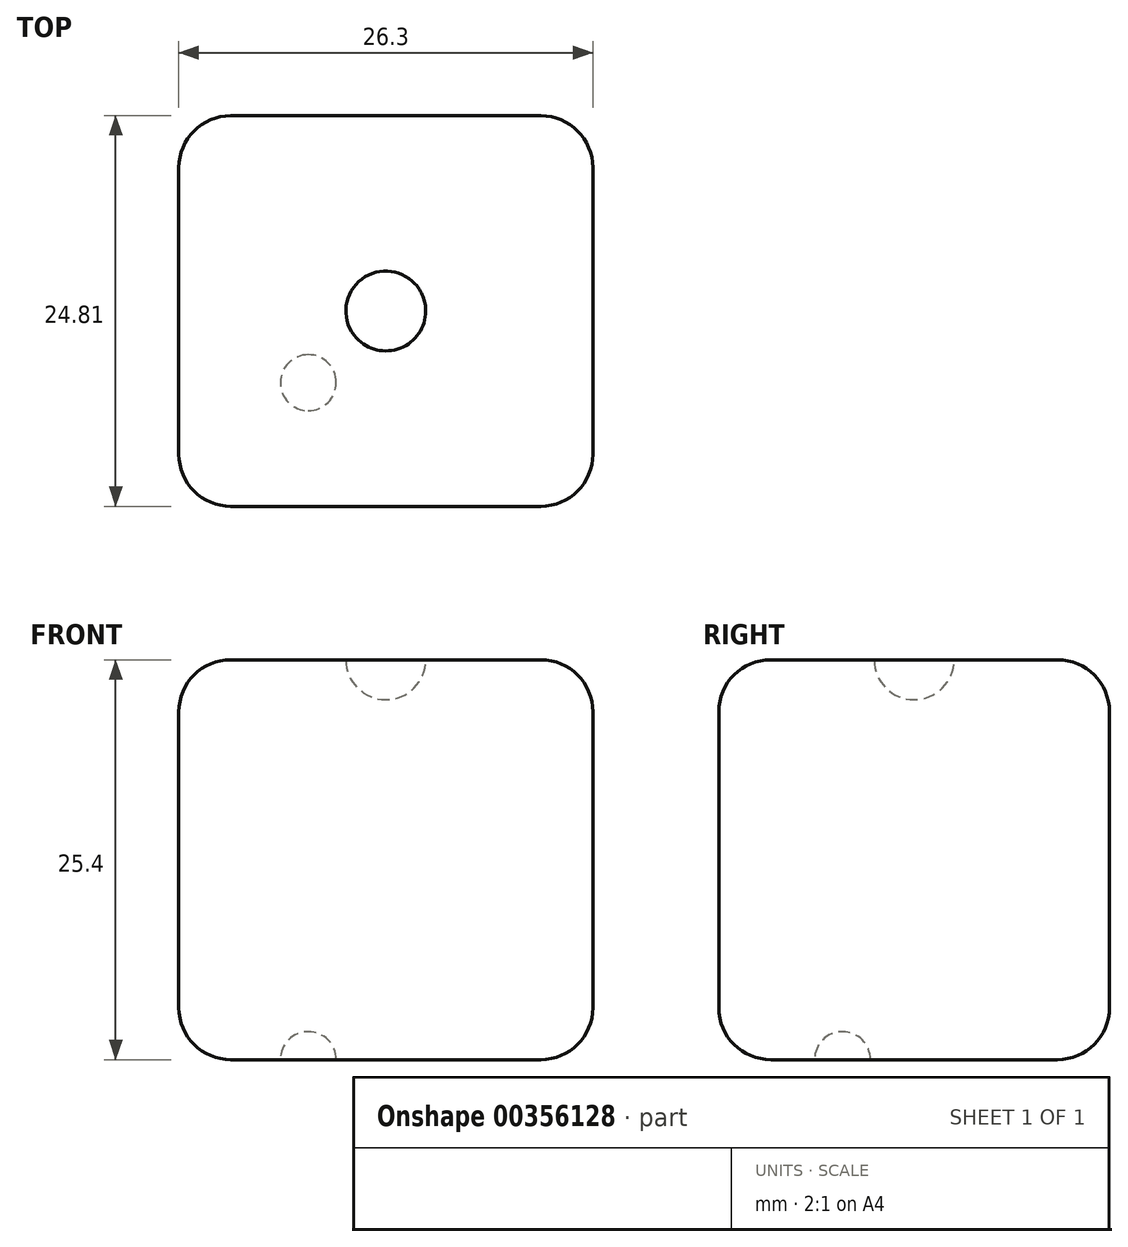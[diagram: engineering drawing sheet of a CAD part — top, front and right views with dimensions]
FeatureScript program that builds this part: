
annotation { "Feature Type Name" : "Feature", "Feature Type Description" : "" }
export const myFeature = defineFeature(function(context is Context, id is Id, definition is map)
    precondition{}
    {
        {
            var Q0;
            Q0=qCreatedBy(makeId("Top.planeOp"),FACE);
            var sketch = newSketch(context, id + "F0", { "sketchPlane" : qUnion([Q0])});
            skLineSegment(sketch, "E0.bottom", {"start": v(35.97, 40.2) * mm, "end": v(62.27, 40.2) * mm});
            skLineSegment(sketch, "E0.top", {"start": v(35.97, 15.4) * mm, "end": v(62.27, 15.4) * mm});
            skLineSegment(sketch, "E0.left", {"start": v(35.97, 40.2) * mm, "end": v(35.97, 15.4) * mm});
            skLineSegment(sketch, "E0.right", {"start": v(62.27, 40.2) * mm, "end": v(62.27, 15.4) * mm});
            skSolve(sketch);
        }
        {
            var Q0;
            Q0=makeQuery(id+"F0.imprint","IMPRINT",FACE,{"disambiguationData":[TD([[makeQuery(id+"F0.imprint","IMPRINT",EDGE,{"derivedFrom":sQuery(id+"F0.wireOp",EDGE,"E0.bottom")}),-1.0]])]});
            extrude(context, id + "F1", {"entities" : qUnion([Q0]), "depth" : 25.4 * mm});
        }
        {
            var Q0;
            Q0=makeQuery(id+"F1.opExtrude","CAP_EDGE",EDGE,{"disambiguationData":[OSD([sQuery(id+"F0.wireOp",EDGE,"E0.top")])],"isStart":false});
            var Q1;
            Q1=makeQuery(id+"F1.opExtrude","CAP_EDGE",EDGE,{"disambiguationData":[OSD([sQuery(id+"F0.wireOp",EDGE,"E0.right")])],"isStart":false});
            var Q2;
            Q2=makeQuery(id+"F1.opExtrude","CAP_EDGE",EDGE,{"disambiguationData":[OSD([sQuery(id+"F0.wireOp",EDGE,"E0.bottom")])],"isStart":false});
            var Q3;
            Q3=makeQuery(id+"F1.opExtrude","CAP_EDGE",EDGE,{"disambiguationData":[OSD([sQuery(id+"F0.wireOp",EDGE,"E0.left")])],"isStart":false});
            var Q4;
            Q4=makeQuery(id+"F1.opExtrude","SWEPT_EDGE",EDGE,{"disambiguationData":[OSD([sQuery(id+"F0.wireOp",EDGE,"E0.bottom"),sQuery(id+"F0.wireOp",EDGE,"E0.right")])]});
            var Q5;
            Q5=makeQuery(id+"F1.opExtrude","CAP_EDGE",EDGE,{"disambiguationData":[OSD([sQuery(id+"F0.wireOp",EDGE,"E0.right")])],"isStart":true});
            var Q6;
            Q6=makeQuery(id+"F1.opExtrude","CAP_EDGE",EDGE,{"disambiguationData":[OSD([sQuery(id+"F0.wireOp",EDGE,"E0.bottom")])],"isStart":true});
            var Q7;
            Q7=makeQuery(id+"F1.opExtrude","SWEPT_EDGE",EDGE,{"disambiguationData":[OSD([sQuery(id+"F0.wireOp",EDGE,"E0.bottom"),sQuery(id+"F0.wireOp",EDGE,"E0.left")])]});
            var Q8;
            Q8=makeQuery(id+"F1.opExtrude","CAP_EDGE",EDGE,{"disambiguationData":[OSD([sQuery(id+"F0.wireOp",EDGE,"E0.top")])],"isStart":true});
            var Q9;
            Q9=makeQuery(id+"F1.opExtrude","CAP_EDGE",EDGE,{"disambiguationData":[OSD([sQuery(id+"F0.wireOp",EDGE,"E0.left")])],"isStart":true});
            var Q10;
            Q10=makeQuery(id+"F1.opExtrude","SWEPT_EDGE",EDGE,{"disambiguationData":[OSD([sQuery(id+"F0.wireOp",EDGE,"E0.top"),sQuery(id+"F0.wireOp",EDGE,"E0.left")])]});
            var Q11;
            Q11=makeQuery(id+"F1.opExtrude","SWEPT_EDGE",EDGE,{"disambiguationData":[OSD([sQuery(id+"F0.wireOp",EDGE,"E0.top"),sQuery(id+"F0.wireOp",EDGE,"E0.right")])]});
            fillet(context, id + "F2", {"entities" : qUnion([Q0, Q1, Q2, Q3, Q4, Q5, Q6, Q7, Q8, Q9, Q10, Q11]), "radius" : 3.3 * mm, "tangentPropagation" : true, "allowEdgeOverflow" : false});
        }
        {
            var Q0;
            Q0=makeQuery(id+"F1.opExtrude","CAP_FACE",FACE,{"disambiguationData":[OSD([sQuery(id+"F0.wireOp",EDGE,"E0.bottom"),sQuery(id+"F0.wireOp",EDGE,"E0.top"),sQuery(id+"F0.wireOp",EDGE,"E0.left"),sQuery(id+"F0.wireOp",EDGE,"E0.right")])],"isStart":false});
            var sketch = newSketch(context, id + "F3", { "sketchPlane" : qUnion([Q0])});
            skLineSegment(sketch, "E1", {"start": v(39.27, 18.7) * mm, "end": v(58.97, 36.9) * mm});
            skCircle(sketch, "E2", {"center": v(49.12, 27.8) * mm, "radius": 2.53 * mm});
            skSolve(sketch);
        }
        {
            var Q0;
            {var subQ0=sQuery(id+"F3.wireOp",EDGE,"E2");var subQ1=sQuery(id+"F3.wireOp",EDGE,"E1");var subQ2=makeQuery(id+"F3.imprint","INTERSECT",VERTEX,{"disambiguationData":[OD(0.0)],"derivedFrom":[subQ1,subQ0]});Q0=makeQuery(id+"F3.imprint","IMPRINT",FACE,{"disambiguationData":[TD([[makeQuery(id+"F3.imprint","IMPRINT",EDGE,{"disambiguationData":[TD([[subQ2,-1.0]])],"derivedFrom":subQ1}),1.0]])]});}
            var Q1;
            Q1=sQuery(id+"F3.wireOp",EDGE,"E1");
            revolve(context, id + "F4", {"operationType" : NewBodyOperationType.REMOVE, "entities" : qUnion([Q0]), "axis" : qUnion([Q1]), "revolveType" : RevolveType.TWO_DIRECTIONS, "angle" : 0 * degree, "angleBack" : 180 * degree});
        }
        {
            var Q0;
            Q0=makeQuery(id+"F1.opExtrude","CAP_FACE",FACE,{"disambiguationData":[OSD([sQuery(id+"F0.wireOp",EDGE,"E0.bottom"),sQuery(id+"F0.wireOp",EDGE,"E0.top"),sQuery(id+"F0.wireOp",EDGE,"E0.left"),sQuery(id+"F0.wireOp",EDGE,"E0.right")])],"isStart":true});
            var sketch = newSketch(context, id + "F5", { "sketchPlane" : qUnion([Q0])});
            skLineSegment(sketch, "E3", {"start": v(39.27, -18.7) * mm, "end": v(49.12, -18.7) * mm});
            skLineSegment(sketch, "E4", {"start": v(49.12, -18.7) * mm, "end": v(58.97, -18.7) * mm});
            skLineSegment(sketch, "E5", {"start": v(39.27, -27.8) * mm, "end": v(58.97, -27.8) * mm});
            skLineSegment(sketch, "E6", {"start": v(44.2, -18.7) * mm, "end": v(44.2, -27.8) * mm});
            skLineSegment(sketch, "E7", {"start": v(44.2, -27.8) * mm, "end": v(44.2, -36.9) * mm});
            skLineSegment(sketch, "E8", {"start": v(54.04, -18.7) * mm, "end": v(54.04, -27.8) * mm});
            skLineSegment(sketch, "E9", {"start": v(54.04, -27.8) * mm, "end": v(54.04, -36.9) * mm});
            skLineSegment(sketch, "E10", {"start": v(39.27, -18.7) * mm, "end": v(39.27, -27.8) * mm});
            skLineSegment(sketch, "E11", {"start": v(39.27, -27.8) * mm, "end": v(39.27, -36.9) * mm});
            skLineSegment(sketch, "E12", {"start": v(39.27, -23.24) * mm, "end": v(44.2, -23.24) * mm});
            skLineSegment(sketch, "E13", {"start": v(44.2, -23.24) * mm, "end": v(54.04, -23.24) * mm});
            skLineSegment(sketch, "E14", {"start": v(54.04, -23.24) * mm, "end": v(58.97, -23.24) * mm});
            skLineSegment(sketch, "E15", {"start": v(39.27, -31.88) * mm, "end": v(44.2, -31.88) * mm});
            skLineSegment(sketch, "E16", {"start": v(44.2, -31.88) * mm, "end": v(54.04, -31.88) * mm});
            skLineSegment(sketch, "E17", {"start": v(54.04, -31.88) * mm, "end": v(58.97, -31.88) * mm});
            skCircle(sketch, "E18", {"center": v(44.2, -23.24) * mm, "radius": 1.78 * mm});
            skCircle(sketch, "E19", {"center": v(44.2, -27.8) * mm, "radius": 1.78 * mm});
            skCircle(sketch, "E20", {"center": v(54.04, -31.88) * mm, "radius": 1.78 * mm});
            skCircle(sketch, "E21", {"center": v(54.04, -23.24) * mm, "radius": 1.78 * mm});
            skLineSegment(sketch, "E22", {"start": v(54.04, -27.8) * mm, "end": v(63.9, -27.8) * mm});
            skCircle(sketch, "E23", {"center": v(53.99, -27.73) * mm, "radius": 1.78 * mm});
            skCircle(sketch, "E24", {"center": v(44.2, -31.88) * mm, "radius": 1.78 * mm});
            skSolve(sketch);
        }
        {
            var Q0;
            {var subQ1=sQuery(id+"F5.wireOp",EDGE,"E6");var subQ3=sQuery(id+"F5.wireOp",EDGE,"E18");var subQ4=makeQuery(id+"F5.imprint","INTERSECT",VERTEX,{"disambiguationData":[OD(1.0)],"derivedFrom":[subQ1,subQ3]});Q0=makeQuery(id+"F5.imprint","IMPRINT",FACE,{"disambiguationData":[TD([[makeQuery(id+"F5.imprint","IMPRINT",EDGE,{"disambiguationData":[TD([[subQ4,1.0]])],"derivedFrom":subQ3}),1.0]])]});}
            var Q1;
            {var subQ1=sQuery(id+"F5.wireOp",EDGE,"E6");var subQ3=sQuery(id+"F5.wireOp",EDGE,"E18");var subQ4=makeQuery(id+"F5.imprint","INTERSECT",VERTEX,{"disambiguationData":[OD(0.0)],"derivedFrom":[subQ1,subQ3]});Q1=makeQuery(id+"F5.imprint","IMPRINT",FACE,{"disambiguationData":[TD([[makeQuery(id+"F5.imprint","IMPRINT",EDGE,{"disambiguationData":[TD([[subQ4,-1.0]])],"derivedFrom":subQ3}),1.0]])]});}
            var Q2;
            Q2=sQuery(id+"F5.wireOp",EDGE,"E6");
            revolve(context, id + "F6", {"operationType" : NewBodyOperationType.REMOVE, "entities" : qUnion([Q0, Q1]), "axis" : qUnion([Q2]), "revolveType" : RevolveType.FULL, "oppositeDirection" : true});
        }
    });
